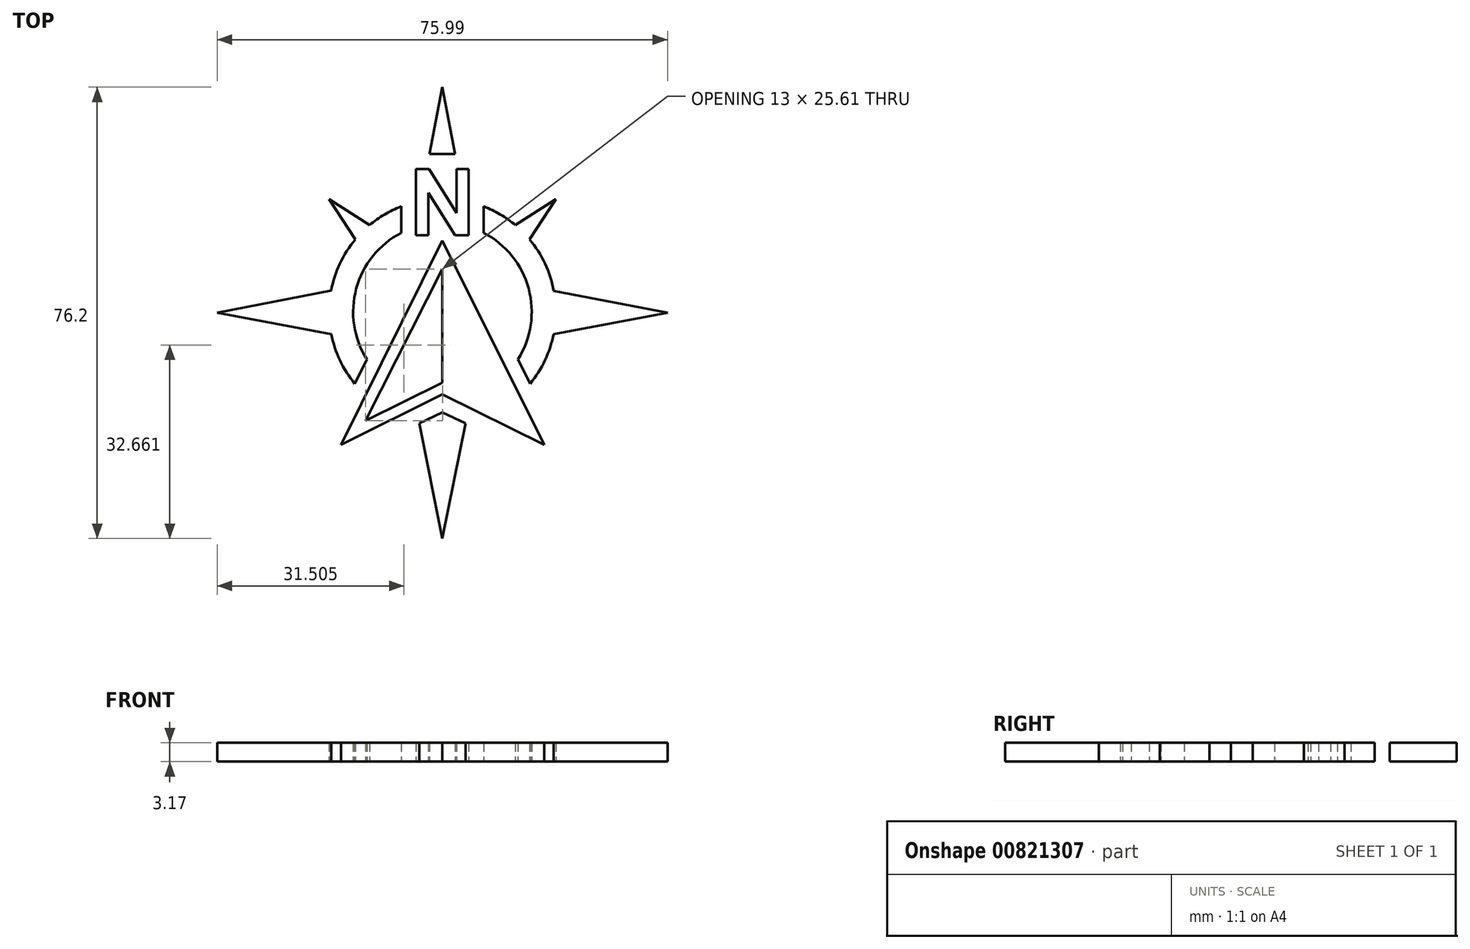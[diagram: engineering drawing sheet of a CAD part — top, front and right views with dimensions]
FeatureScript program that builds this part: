
annotation { "Feature Type Name" : "Feature", "Feature Type Description" : "" }
export const myFeature = defineFeature(function(context is Context, id is Id, definition is map)
    precondition{}
    {
        {
            var Q0;
            Q0=qCreatedBy(makeId("Top.planeOp"),FACE);
            var sketch = newSketch(context, id + "F0", { "sketchPlane" : qUnion([Q0])});
            skLineSegment(sketch, "E0", {"start": v(0, 38.1) * mm, "end": v(19.24, 34.52) * mm});
            skLineSegment(sketch, "E1", {"start": v(0, 38.1) * mm, "end": v(19.21, 41.82) * mm});
            skLineSegment(sketch, "E2", {"start": v(75.99, 38.1) * mm, "end": v(56.8, 41.82) * mm});
            skLineSegment(sketch, "E3", {"start": v(75.99, 38.1) * mm, "end": v(56.77, 34.52) * mm});
            skArc(sketch, "E4", {"start": v(31.03, 56.06) * mm, "mid": v(28.23, 54.7) * mm, "end": v(25.7, 52.89) * mm});
            skArc(sketch, "E5", {"start": v(31.03, 51.6) * mm, "mid": v(23.46, 42.19) * mm, "end": v(25.24, 30.24) * mm});
            skLineSegment(sketch, "E6", {"start": v(20.88, 15.83) * mm, "end": v(38, 50.3) * mm});
            skLineSegment(sketch, "E7", {"start": v(38, 50.3) * mm, "end": v(55.2, 15.83) * mm});
            skLineSegment(sketch, "E8", {"start": v(38, 24.34) * mm, "end": v(20.88, 15.83) * mm});
            skLineSegment(sketch, "E9", {"start": v(38, 24.34) * mm, "end": v(55.2, 15.83) * mm});
            skLineSegment(sketch, "E10", {"start": v(31.03, 56.06) * mm, "end": v(31.03, 51.6) * mm});
            skLineSegment(sketch, "E11", {"start": v(25.24, 30.24) * mm, "end": v(23.2, 26.13) * mm});
            skLineSegment(sketch, "E12.MirrorCS", {"start": v(44.98, 56.06) * mm, "end": v(44.98, 51.6) * mm});
            skLineSegment(sketch, "E13.MirrorCS", {"start": v(50.77, 30.24) * mm, "end": v(52.8, 26.13) * mm});
            skArc(sketch, "E14.trimOffspring", {"start": v(50.77, 30.24) * mm, "mid": v(52.55, 42.19) * mm, "end": v(44.98, 51.6) * mm});
            skArc(sketch, "E15.trimOffspring", {"start": v(52.8, 26.13) * mm, "mid": v(55.3, 30.08) * mm, "end": v(56.77, 34.52) * mm});
            skArc(sketch, "E16.trimOffspring", {"start": v(19.24, 34.52) * mm, "mid": v(20.7, 30.08) * mm, "end": v(23.2, 26.13) * mm});
            skLineSegment(sketch, "E17.trimOffspring", {"start": v(23.6, 42.68) * mm, "end": v(38, 45.47) * mm, "construction": true});
            skLineSegment(sketch, "E18.trimOffspring", {"start": v(23.64, 33.7) * mm, "end": v(38, 31.03) * mm, "construction": true});
            skLineSegment(sketch, "E19.trimOffspring", {"start": v(52.37, 33.7) * mm, "end": v(38, 31.03) * mm, "construction": true});
            skLineSegment(sketch, "E20.trimOffspring", {"start": v(52.4, 42.67) * mm, "end": v(38, 45.47) * mm, "construction": true});
            skArc(sketch, "E21.trimOffspring", {"start": v(56.8, 41.82) * mm, "mid": v(55.3, 46.4) * mm, "end": v(52.72, 50.47) * mm});
            skLineSegment(sketch, "E22", {"start": v(23.29, 50.47) * mm, "end": v(18.88, 57.29) * mm});
            skLineSegment(sketch, "E23", {"start": v(18.88, 57.29) * mm, "end": v(25.7, 52.89) * mm});
            skLineSegment(sketch, "E24.MirrorCS", {"start": v(52.72, 50.47) * mm, "end": v(57.13, 57.29) * mm});
            skLineSegment(sketch, "E25.MirrorCS", {"start": v(57.13, 57.29) * mm, "end": v(50.32, 52.89) * mm});
            skArc(sketch, "E26.trimOffspring", {"start": v(23.29, 50.47) * mm, "mid": v(20.7, 46.4) * mm, "end": v(19.21, 41.82) * mm});
            skArc(sketch, "E27.trimOffspring", {"start": v(50.32, 52.89) * mm, "mid": v(47.78, 54.7) * mm, "end": v(44.98, 56.06) * mm});
            skLineSegment(sketch, "E28", {"start": v(38, 26.3) * mm, "end": v(25, 19.85) * mm});
            skLineSegment(sketch, "E29", {"start": v(25, 19.85) * mm, "end": v(38, 45.47) * mm});
            skLineSegment(sketch, "E30", {"start": v(38, 45.47) * mm, "end": v(38, 26.3) * mm});
            skLineSegment(sketch, "E31", {"start": v(35.83, 64.9) * mm, "end": v(40.14, 64.9) * mm});
            skLineSegment(sketch, "E32", {"start": v(38, 76.2) * mm, "end": v(35.83, 64.9) * mm});
            skLineSegment(sketch, "E33", {"start": v(38, 76.2) * mm, "end": v(40.14, 64.9) * mm});
            skLineSegment(sketch, "E34", {"start": v(38, 0) * mm, "end": v(41.9, 19.42) * mm});
            skLineSegment(sketch, "E35", {"start": v(41.9, 19.42) * mm, "end": v(38, 21.26) * mm});
            skLineSegment(sketch, "E36", {"start": v(38, 21.26) * mm, "end": v(38, 0) * mm, "construction": true});
            skLineSegment(sketch, "E37.MirrorCS", {"start": v(34.1, 19.42) * mm, "end": v(38, 21.26) * mm});
            skLineSegment(sketch, "E38.MirrorCS", {"start": v(38, 0) * mm, "end": v(34.1, 19.42) * mm});
            skLineSegment(sketch, "E39", {"start": v(33.55, 51.16) * mm, "end": v(33.55, 62.36) * mm});
            skLineSegment(sketch, "E40", {"start": v(33.55, 62.36) * mm, "end": v(35.72, 62.36) * mm});
            skLineSegment(sketch, "E41", {"start": v(42.44, 62.36) * mm, "end": v(42.44, 51.16) * mm});
            skLineSegment(sketch, "E42", {"start": v(42.44, 51.16) * mm, "end": v(40.16, 51.16) * mm});
            skLineSegment(sketch, "E43", {"start": v(35.65, 51.16) * mm, "end": v(35.65, 58.36) * mm});
            skLineSegment(sketch, "E44", {"start": v(35.65, 58.36) * mm, "end": v(40.16, 51.16) * mm});
            skLineSegment(sketch, "E45", {"start": v(40.37, 62.36) * mm, "end": v(40.37, 54.92) * mm});
            skLineSegment(sketch, "E46", {"start": v(40.37, 54.92) * mm, "end": v(35.72, 62.36) * mm});
            skLineSegment(sketch, "E47.trimOffspring", {"start": v(40.37, 62.36) * mm, "end": v(42.44, 62.36) * mm});
            skLineSegment(sketch, "E48.trimOffspring", {"start": v(35.65, 51.16) * mm, "end": v(33.55, 51.16) * mm});
            skSolve(sketch);
        }
        {
            var Q0;
            Q0=makeQuery(id+"F0.imprint","IMPRINT",FACE,{"disambiguationData":[TD([[makeQuery(id+"F0.imprint","IMPRINT",EDGE,{"derivedFrom":sQuery(id+"F0.wireOp",EDGE,"E39")}),-1.0]])]});
            var Q1;
            Q1=makeQuery(id+"F0.imprint","IMPRINT",FACE,{"disambiguationData":[TD([[makeQuery(id+"F0.imprint","IMPRINT",EDGE,{"derivedFrom":sQuery(id+"F0.wireOp",EDGE,"E31")}),1.0]])]});
            var Q2;
            Q2=makeQuery(id+"F0.imprint","IMPRINT",FACE,{"disambiguationData":[TD([[makeQuery(id+"F0.imprint","IMPRINT",EDGE,{"derivedFrom":sQuery(id+"F0.wireOp",EDGE,"E2")}),1.0]])]});
            var Q3;
            Q3=makeQuery(id+"F0.imprint","IMPRINT",FACE,{"disambiguationData":[TD([[makeQuery(id+"F0.imprint","IMPRINT",EDGE,{"derivedFrom":sQuery(id+"F0.wireOp",EDGE,"E6")}),-1.0]])]});
            var Q4;
            Q4=makeQuery(id+"F0.imprint","IMPRINT",FACE,{"disambiguationData":[TD([[makeQuery(id+"F0.imprint","IMPRINT",EDGE,{"derivedFrom":sQuery(id+"F0.wireOp",EDGE,"E34")}),1.0]])]});
            var Q5;
            Q5=makeQuery(id+"F0.imprint","IMPRINT",FACE,{"disambiguationData":[TD([[makeQuery(id+"F0.imprint","IMPRINT",EDGE,{"derivedFrom":sQuery(id+"F0.wireOp",EDGE,"E0")}),1.0]])]});
            extrude(context, id + "F1", {"entities" : qUnion([Q0, Q1, Q2, Q3, Q4, Q5]), "depth" : 3.17 * mm, "offsetDistance" : 25.4 * mm});
        }
    });
